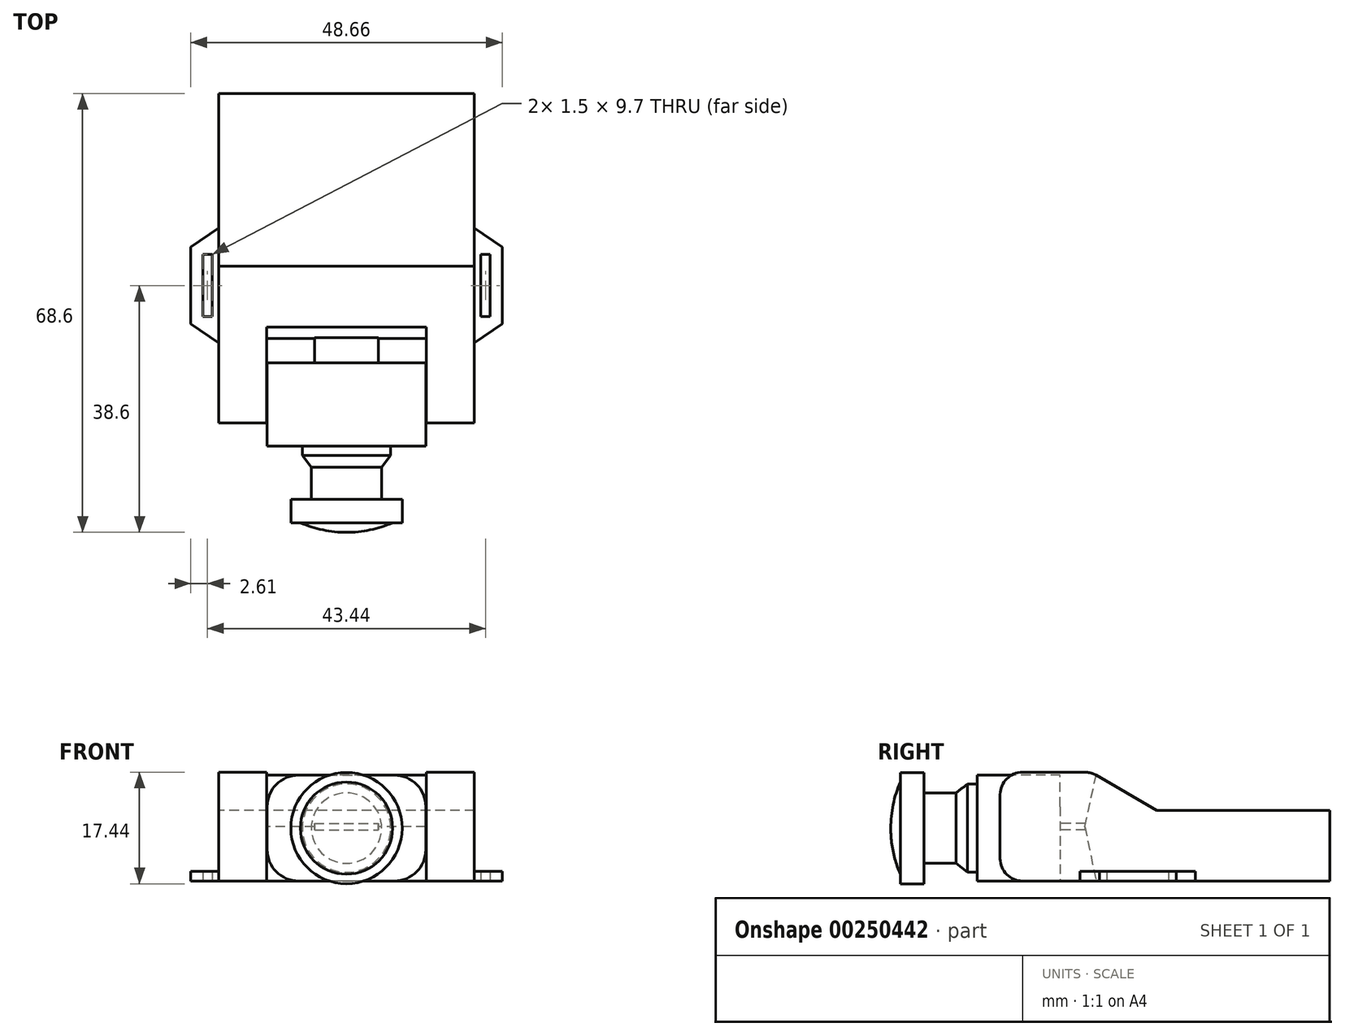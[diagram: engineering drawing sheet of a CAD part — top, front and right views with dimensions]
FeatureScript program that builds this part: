
annotation { "Feature Type Name" : "Feature", "Feature Type Description" : "" }
export const myFeature = defineFeature(function(context is Context, id is Id, definition is map)
    precondition{}
    {
        {
            var Q0;
            Q0=qCreatedBy(makeId("Right.planeOp"),FACE);
            var sketch = newSketch(context, id + "F0", { "sketchPlane" : qUnion([Q0])});
            skLineSegment(sketch, "E0.bottom", {"start": v(25.75, 11) * mm, "end": v(-1.25, 11) * mm});
            skLineSegment(sketch, "E0.top", {"start": v(25.75, 0) * mm, "end": v(-22.25, 0) * mm});
            skLineSegment(sketch, "E0.left", {"start": v(25.75, 11) * mm, "end": v(25.75, 0) * mm});
            skLineSegment(sketch, "E1", {"start": v(-25.75, 3.5) * mm, "end": v(-25.75, 13.5) * mm});
            skLineSegment(sketch, "E2", {"start": v(-22.25, 17) * mm, "end": v(-12.5, 17) * mm});
            skLineSegment(sketch, "E3", {"start": v(-10.75, 16.53) * mm, "end": v(-1.25, 11) * mm});
            skArc(sketch, "E4", {"start": v(-10.75, 16.53) * mm, "mid": v(-11.6, 16.88) * mm, "end": v(-12.5, 17) * mm});
            skArc(sketch, "E5", {"start": v(-25.75, 3.5) * mm, "mid": v(-24.72, 1.03) * mm, "end": v(-22.25, 0) * mm});
            skArc(sketch, "E6", {"start": v(-22.25, 17) * mm, "mid": v(-24.72, 15.97) * mm, "end": v(-25.75, 13.5) * mm});
            skSolve(sketch);
        }
        {
            var Q0;
            Q0=makeQuery(id+"F0.imprint","IMPRINT",FACE,{"disambiguationData":[TD([[makeQuery(id+"F0.imprint","IMPRINT",EDGE,{"derivedFrom":sQuery(id+"F0.wireOp",EDGE,"E0.bottom")}),1.0]])]});
            extrude(context, id + "F1", {"entities" : qUnion([Q0]), "endBound" : BoundingType.SYMMETRIC, "depth" : 40 * mm});
        }
        {
            var Q0;
            Q0=makeQuery(id+"F1.opExtrude","SWEPT_FACE",FACE,{"disambiguationData":[OSD([sQuery(id+"F0.wireOp",EDGE,"E2")])]});
            var sketch = newSketch(context, id + "F2", { "sketchPlane" : qUnion([Q0])});
            skLineSegment(sketch, "E7.bottom", {"start": v(-12.5, -12.5) * mm, "end": v(0, -12.5) * mm});
            skLineSegment(sketch, "E7.top", {"start": v(-12.5, -25.75) * mm, "end": v(0, -25.75) * mm});
            skLineSegment(sketch, "E7.left", {"start": v(-12.5, -12.5) * mm, "end": v(-12.5, -25.75) * mm});
            skLineSegment(sketch, "E7.right", {"start": v(12.5, -12.5) * mm, "end": v(12.5, -25.75) * mm});
            skLineSegment(sketch, "E8", {"start": v(0, -12.5) * mm, "end": v(12.5, -12.5) * mm});
            skLineSegment(sketch, "E9", {"start": v(0, -25.75) * mm, "end": v(12.5, -25.75) * mm});
            skLineSegment(sketch, "E10.0.1", {"start": v(-20, -25.75) * mm, "end": v(20, -25.75) * mm, "construction": true});
            skLineSegment(sketch, "E10.0.3", {"start": v(20, -25.75) * mm, "end": v(-20, -25.75) * mm});
            skLineSegment(sketch, "E11.0", {"start": v(20, -12.5) * mm, "end": v(-20, -12.5) * mm, "construction": true});
            skSolve(sketch);
        }
        {
            var Q0;
            Q0 = qSketchRegion(id + "F2", true);
            var Q1;
            Q1=makeQuery(id+"F1.opExtrude","SWEPT_FACE",FACE,{"disambiguationData":[OSD([sQuery(id+"F0.wireOp",EDGE,"E0.top")])]});
            extrude(context, id + "F3", {"entities" : qUnion([Q0]), "operationType" : NewBodyOperationType.REMOVE, "endBound" : BoundingType.UP_TO_SURFACE, "oppositeDirection" : true, "endBoundEntityFace" : qUnion([Q1]), "depth" : 25 * mm});
        }
        {
            var Q0;
            Q0=makeQuery(id+"F3.boolean.opBoolean","COPY",FACE,{"derivedFrom":makeQuery(id+"F3.opExtrude","SWEPT_FACE",FACE,{"disambiguationData":[OSD([sQuery(id+"F2.wireOp",EDGE,"E7.left")])]})});
            var sketch = newSketch(context, id + "F4", { "sketchPlane" : qUnion([Q0])});
            skPoint(sketch, "E12.0", {"position": v(-10.75, 16.53) * mm});
            skPoint(sketch, "E12.1", {"position": v(-12.5, 17) * mm});
            skPoint(sketch, "E12.2", {"position": v(-12.5, 0) * mm});
            skLineSegment(sketch, "E13", {"start": v(-10.75, 16.53) * mm, "end": v(-12.5, 8.5) * mm});
            skLineSegment(sketch, "E14", {"start": v(-12.5, 8.5) * mm, "end": v(-10.75, 0) * mm});
            skLineSegment(sketch, "E15", {"start": v(-10.75, 0) * mm, "end": v(-12.5, 0) * mm});
            skLineSegment(sketch, "E16", {"start": v(-12.5, 0) * mm, "end": v(-12.5, 8.5) * mm});
            skLineSegment(sketch, "E17", {"start": v(-12.5, 8.5) * mm, "end": v(-12.5, 17) * mm});
            skPoint(sketch, "E18.0", {"position": v(-11.6, 16.88) * mm});
            skArc(sketch, "E19.converted", {"start": v(-12.5, 17) * mm, "mid": v(-11.6, 16.88) * mm, "end": v(-10.75, 16.53) * mm});
            skSolve(sketch);
        }
        {
            var Q0;
            Q0 = qSketchRegion(id + "F4", true);
            var Q1;
            Q1=makeQuery(id+"F3.boolean.opBoolean","COPY",FACE,{"derivedFrom":makeQuery(id+"F3.opExtrude","SWEPT_FACE",FACE,{"disambiguationData":[OSD([sQuery(id+"F2.wireOp",EDGE,"E7.right")])]})});
            extrude(context, id + "F5", {"entities" : qUnion([Q0]), "operationType" : NewBodyOperationType.REMOVE, "endBound" : BoundingType.UP_TO_SURFACE, "endBoundEntityFace" : qUnion([Q1]), "depth" : 25 * mm});
        }
        {
            var Q0;
            Q0=makeQuery(id+"F1.opExtrude","SWEPT_FACE",FACE,{"disambiguationData":[OSD([sQuery(id+"F0.wireOp",EDGE,"E0.top")])]});
            var sketch = newSketch(context, id + "F6", { "sketchPlane" : qUnion([Q0])});
            skLineSegment(sketch, "E20.0", {"start": v(-20, -4.75) * mm, "end": v(-20, 13.25) * mm});
            skLineSegment(sketch, "E21", {"start": v(-20, 13.25) * mm, "end": v(-24.33, 10.25) * mm});
            skLineSegment(sketch, "E22", {"start": v(-24.33, 10.25) * mm, "end": v(-24.33, 4.25) * mm});
            skLineSegment(sketch, "E23", {"start": v(-24.33, -1.75) * mm, "end": v(-20, -4.75) * mm});
            skLineSegment(sketch, "E24.bottom", {"start": v(-22.47, 9.1) * mm, "end": v(-20.97, 9.1) * mm});
            skLineSegment(sketch, "E24.top", {"start": v(-22.47, -0.6) * mm, "end": v(-20.97, -0.6) * mm});
            skLineSegment(sketch, "E24.left", {"start": v(-22.47, 9.1) * mm, "end": v(-22.47, 4.25) * mm});
            skLineSegment(sketch, "E24.right", {"start": v(-20.97, 9.1) * mm, "end": v(-20.97, 4.25) * mm});
            skLineSegment(sketch, "E25", {"start": v(-24.33, 4.25) * mm, "end": v(-24.33, -1.75) * mm});
            skLineSegment(sketch, "E26", {"start": v(-22.47, 4.25) * mm, "end": v(-22.47, -0.6) * mm});
            skLineSegment(sketch, "E27", {"start": v(-20.97, 4.25) * mm, "end": v(-20.97, -0.6) * mm});
            skLineSegment(sketch, "E28", {"start": v(-24.33, 4.25) * mm, "end": v(-22.47, 4.25) * mm, "construction": true});
            skPoint(sketch, "E29.orphan", {"position": v(-20, 22.25) * mm});
            skPoint(sketch, "E30.orphan", {"position": v(-20, -25.75) * mm});
            skSolve(sketch);
        }
        {
            var Q0;
            Q0 = qSketchRegion(id + "F6", true);
            extrude(context, id + "F7", {"entities" : qUnion([Q0]), "oppositeDirection" : true, "depth" : 1.5 * mm});
        }
        {
            var Q0;
            Q0=makeQuery(id+"F7.opExtrude","SWEPT_BODY",BODY,{"disambiguationData":[OSD([sQuery(id+"F6.wireOp",EDGE,"E20.0"),sQuery(id+"F6.wireOp",EDGE,"E21"),sQuery(id+"F6.wireOp",EDGE,"E22"),sQuery(id+"F6.wireOp",EDGE,"E23"),sQuery(id+"F6.wireOp",EDGE,"E24.bottom"),sQuery(id+"F6.wireOp",EDGE,"E24.top"),sQuery(id+"F6.wireOp",EDGE,"E24.left"),sQuery(id+"F6.wireOp",EDGE,"E24.right"),sQuery(id+"F6.wireOp",EDGE,"E25"),sQuery(id+"F6.wireOp",EDGE,"E26"),sQuery(id+"F6.wireOp",EDGE,"E27")])]});
            var Q1;
            Q1=qCreatedBy(makeId("Right.planeOp"),FACE);
            mirror(context, id + "F8", {"operationType" : NewBodyOperationType.ADD, "entities" : qUnion([Q0]), "mirrorPlane" : qUnion([Q1])});
        }
        {
            var Q0;
            {var subQ2=sQuery(id+"F0.wireOp",EDGE,"E1");Q0=makeQuery(id+"F3.boolean.opBoolean","SPLIT",FACE,{"disambiguationData":[TD([makeQuery(id+"F3.opExtrude","SWEPT_FACE",FACE,{"disambiguationData":[OSD([sQuery(id+"F2.wireOp",EDGE,"E7.right")])]})])],"derivedFrom":makeQuery(id+"F1.opExtrude","SWEPT_FACE",FACE,{"disambiguationData":[OSD([subQ2])]})});}
            cPlane(context, id + "F9", {"entities" : qUnion([Q0]), "cplaneType" : CPlaneType.OFFSET, "offset" : 3.6 * mm, "width" : 150 * mm, "height" : 150 * mm});
        }
        {
            var Q0;
            Q0=qCreatedBy(id+"F9.planeOp",FACE);
            var sketch = newSketch(context, id + "F10", { "sketchPlane" : qUnion([Q0])});
            skLineSegment(sketch, "E31.bottom", {"start": v(-12.4, 16.53) * mm, "end": v(0, 16.53) * mm});
            skLineSegment(sketch, "E31.top", {"start": v(-12.4, 0) * mm, "end": v(0, 0) * mm});
            skLineSegment(sketch, "E31.left", {"start": v(-12.4, 11.63) * mm, "end": v(-12.4, 4.9) * mm});
            skLineSegment(sketch, "E31.right", {"start": v(12.4, 11.63) * mm, "end": v(12.4, 4.9) * mm});
            skArc(sketch, "E32", {"start": v(-7.5, 16.53) * mm, "mid": v(-10.96, 15.1) * mm, "end": v(-12.4, 11.63) * mm});
            skArc(sketch, "E33", {"start": v(12.4, 11.63) * mm, "mid": v(10.96, 15.1) * mm, "end": v(7.5, 16.53) * mm});
            skArc(sketch, "E34", {"start": v(7.5, 0) * mm, "mid": v(10.96, 1.44) * mm, "end": v(12.4, 4.9) * mm});
            skArc(sketch, "E35", {"start": v(-12.4, 4.9) * mm, "mid": v(-10.96, 1.44) * mm, "end": v(-7.5, 0) * mm});
            skLineSegment(sketch, "E36.0", {"start": v(12.5, 16.53) * mm, "end": v(12.4, 16.53) * mm, "construction": true});
            skLineSegment(sketch, "E36.1", {"start": v(12.5, 0) * mm, "end": v(12.4, 0) * mm, "construction": true});
            skLineSegment(sketch, "E37", {"start": v(0, 16.53) * mm, "end": v(-7.5, 16.53) * mm, "construction": true});
            skLineSegment(sketch, "E38", {"start": v(0, 0) * mm, "end": v(-7.5, 0) * mm, "construction": true});
            skLineSegment(sketch, "E39", {"start": v(0, 16.53) * mm, "end": v(12.4, 16.53) * mm});
            skLineSegment(sketch, "E40", {"start": v(0, 0) * mm, "end": v(12.4, 0) * mm});
            skLineSegment(sketch, "E41.trimOffspring", {"start": v(-12.4, 16.53) * mm, "end": v(-12.5, 16.53) * mm, "construction": true});
            skLineSegment(sketch, "E42.trimOffspring", {"start": v(7.5, 16.53) * mm, "end": v(0, 16.53) * mm, "construction": true});
            skLineSegment(sketch, "E43.trimOffspring", {"start": v(7.5, 0) * mm, "end": v(0, 0) * mm, "construction": true});
            skLineSegment(sketch, "E44.trimOffspring", {"start": v(-12.4, 0) * mm, "end": v(-12.5, 0) * mm, "construction": true});
            skSolve(sketch);
        }
        {
            var Q0;
            Q0 = qSketchRegion(id + "F10", true);
            extrude(context, id + "F11", {"entities" : qUnion([Q0]), "oppositeDirection" : true, "depth" : 13 * mm});
        }
        {
            var Q0;
            Q0=makeQuery(id+"F11.opExtrude","CAP_FACE",FACE,{"disambiguationData":[OSD([sQuery(id+"F10.wireOp",EDGE,"E31.bottom"),sQuery(id+"F10.wireOp",EDGE,"E31.top"),sQuery(id+"F10.wireOp",EDGE,"E31.left"),sQuery(id+"F10.wireOp",EDGE,"E31.right"),sQuery(id+"F10.wireOp",EDGE,"E32"),sQuery(id+"F10.wireOp",EDGE,"E33"),sQuery(id+"F10.wireOp",EDGE,"E34"),sQuery(id+"F10.wireOp",EDGE,"E35"),sQuery(id+"F10.wireOp",EDGE,"E39"),sQuery(id+"F10.wireOp",EDGE,"E40")])],"isStart":false});
            var sketch = newSketch(context, id + "F12", { "sketchPlane" : qUnion([Q0])});
            skLineSegment(sketch, "E45.0", {"start": v(-12.5, 8.5) * mm, "end": v(12.5, 8.5) * mm, "construction": true});
            skPoint(sketch, "E46.0", {"position": v(0, 16.53) * mm});
            skPoint(sketch, "E46.1", {"position": v(0, 0) * mm});
            skLineSegment(sketch, "E47.bottom", {"start": v(-5, 9) * mm, "end": v(0, 9) * mm});
            skLineSegment(sketch, "E47.top", {"start": v(-5, 8) * mm, "end": v(0, 8) * mm});
            skLineSegment(sketch, "E47.left", {"start": v(-5, 9) * mm, "end": v(-5, 8.5) * mm});
            skLineSegment(sketch, "E47.right", {"start": v(5, 9) * mm, "end": v(5, 8.5) * mm});
            skLineSegment(sketch, "E48", {"start": v(0, 9) * mm, "end": v(5, 9) * mm});
            skLineSegment(sketch, "E49", {"start": v(0, 8) * mm, "end": v(5, 8) * mm});
            skLineSegment(sketch, "E50", {"start": v(-5, 8.5) * mm, "end": v(-5, 8) * mm});
            skLineSegment(sketch, "E51", {"start": v(5, 8.5) * mm, "end": v(5, 8) * mm});
            skLineSegment(sketch, "E52", {"start": v(0, 16.53) * mm, "end": v(0, 0) * mm, "construction": true});
            skSolve(sketch);
        }
        {
            var Q0;
            Q0 = qSketchRegion(id + "F12", true);
            var Q1;
            Q1=makeQuery(id+"F1.opExtrude","SWEPT_FACE",FACE,{"disambiguationData":[OSD([sQuery(id+"F0.wireOp",EDGE,"E0.left")])]});
            extrude(context, id + "F13", {"entities" : qUnion([Q0]), "operationType" : NewBodyOperationType.ADD, "endBound" : BoundingType.UP_TO_SURFACE, "endBoundEntityFace" : qUnion([Q1]), "depth" : 25 * mm});
        }
        {
            var Q0;
            Q0=qCreatedBy(makeId("Right.planeOp"),FACE);
            var sketch = newSketch(context, id + "F14", { "sketchPlane" : qUnion([Q0])});
            skLineSegment(sketch, "E53.0.0", {"start": v(-29.35, 11.63) * mm, "end": v(-29.35, 4.9) * mm});
            skLineSegment(sketch, "E53.0.1", {"start": v(-29.35, 4.9) * mm, "end": v(-29.35, 0) * mm});
            skLineSegment(sketch, "E53.0.3", {"start": v(-29.35, 0) * mm, "end": v(-29.35, 4.9) * mm, "construction": true});
            skLineSegment(sketch, "E53.0.4", {"start": v(-29.35, 4.9) * mm, "end": v(-29.35, 11.63) * mm, "construction": true});
            skLineSegment(sketch, "E53.0.5", {"start": v(-29.35, 11.63) * mm, "end": v(-29.35, 16.53) * mm});
            skLineSegment(sketch, "E53.0.7", {"start": v(-29.35, 16.53) * mm, "end": v(-29.35, 11.63) * mm, "construction": true});
            skLineSegment(sketch, "E54", {"start": v(-29.35, 8.26) * mm, "end": v(-41.35, 8.26) * mm});
            skPoint(sketch, "E54.endSnap0", {"position": v(-29.35, 8.26) * mm});
            skLineSegment(sketch, "E55", {"start": v(-41.35, 8.26) * mm, "end": v(-41.35, 1.06) * mm, "construction": true});
            skLineSegment(sketch, "E56", {"start": v(-41.35, 1.06) * mm, "end": v(-41.35, -0.44) * mm});
            skLineSegment(sketch, "E57", {"start": v(-41.35, -0.44) * mm, "end": v(-37.65, -0.44) * mm});
            skLineSegment(sketch, "E58", {"start": v(-37.65, -0.44) * mm, "end": v(-37.65, 2.76) * mm});
            skLineSegment(sketch, "E59", {"start": v(-37.65, 2.76) * mm, "end": v(-32.65, 2.76) * mm});
            skLineSegment(sketch, "E60", {"start": v(-32.65, 2.76) * mm, "end": v(-30.85, 1.36) * mm});
            skLineSegment(sketch, "E61", {"start": v(-30.85, 1.36) * mm, "end": v(-29.35, 1.36) * mm});
            skLineSegment(sketch, "E62", {"start": v(-29.35, 1.36) * mm, "end": v(-29.35, 8.26) * mm});
            skArc(sketch, "E63", {"start": v(-42.85, 8.26) * mm, "mid": v(-42.47, 4.59) * mm, "end": v(-41.35, 1.06) * mm});
            skLineSegment(sketch, "E64", {"start": v(-41.35, 8.26) * mm, "end": v(-42.85, 8.26) * mm});
            skSolve(sketch);
        }
        {
            var Q0;
            Q0=makeQuery(id+"F14.imprint","IMPRINT",FACE,{"disambiguationData":[TD([[makeQuery(id+"F14.imprint","IMPRINT",EDGE,{"derivedFrom":sQuery(id+"F14.wireOp",EDGE,"E54")}),1.0]])]});
            var Q1;
            Q1=sQuery(id+"F14.wireOp",EDGE,"E54");
            revolve(context, id + "F15", {"operationType" : NewBodyOperationType.ADD, "entities" : qUnion([Q0]), "axis" : qUnion([Q1]), "revolveType" : RevolveType.FULL});
        }
    });
